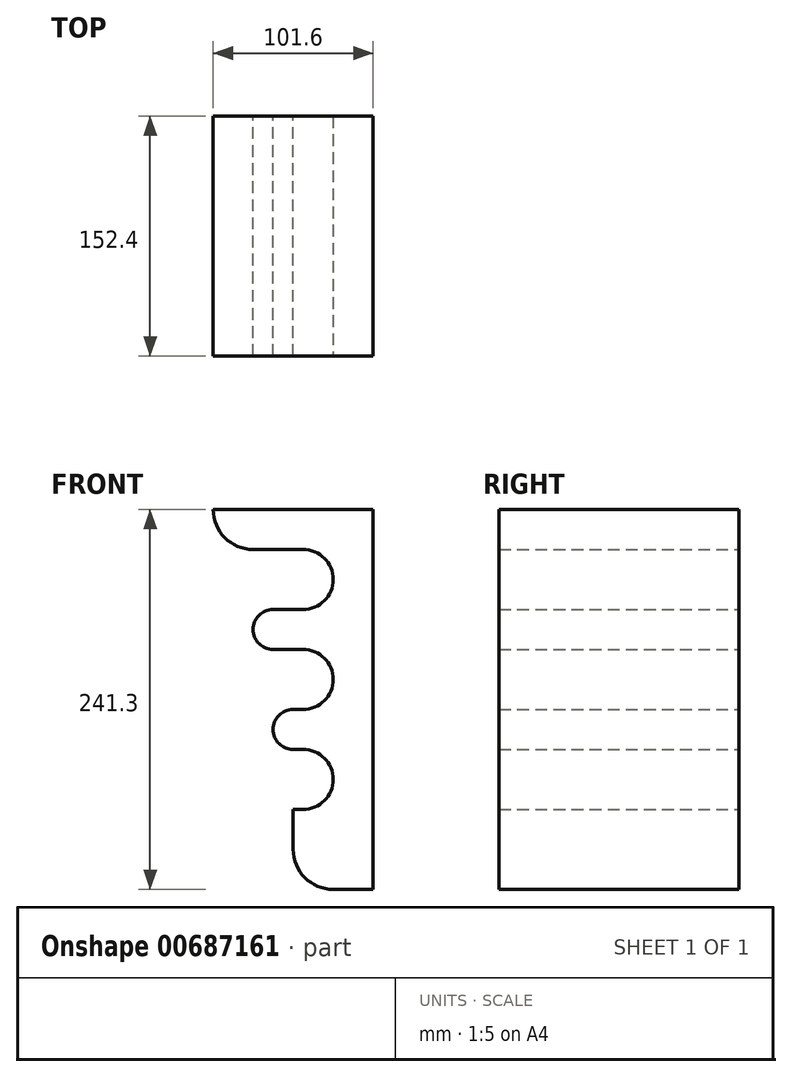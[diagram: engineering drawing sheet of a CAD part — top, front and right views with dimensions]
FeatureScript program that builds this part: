
annotation { "Feature Type Name" : "Feature", "Feature Type Description" : "" }
export const myFeature = defineFeature(function(context is Context, id is Id, definition is map)
    precondition{}
    {
        {
            var Q0;
            Q0=qCreatedBy(makeId("Front.planeOp"),FACE);
            var sketch = newSketch(context, id + "F0", { "sketchPlane" : qUnion([Q0])});
            skLineSegment(sketch, "E0.bottom", {"start": v(-172.92, 215.9) * mm, "end": v(-147.52, 215.9) * mm});
            skLineSegment(sketch, "E0.top", {"start": v(-172.92, 0) * mm, "end": v(-147.52, 0) * mm});
            skLineSegment(sketch, "E0.left", {"start": v(-172.92, 190.5) * mm, "end": v(-172.92, 152.4) * mm});
            skLineSegment(sketch, "E0.right", {"start": v(-147.52, 215.9) * mm, "end": v(-147.52, 0) * mm});
            skLineSegment(sketch, "E1.bottom", {"start": v(-147.52, 215.9) * mm, "end": v(-249.12, 215.9) * mm});
            skLineSegment(sketch, "E1.top", {"start": v(-172.92, 190.5) * mm, "end": v(-249.12, 190.5) * mm});
            skLineSegment(sketch, "E1.left", {"start": v(-147.52, 215.9) * mm, "end": v(-147.52, 190.5) * mm});
            skLineSegment(sketch, "E1.right", {"start": v(-249.12, 215.9) * mm, "end": v(-249.12, 190.5) * mm});
            skLineSegment(sketch, "E2.bottom", {"start": v(-172.92, 152.4) * mm, "end": v(-223.72, 152.4) * mm});
            skLineSegment(sketch, "E2.top", {"start": v(-172.92, 127) * mm, "end": v(-223.72, 127) * mm});
            skLineSegment(sketch, "E2.left", {"start": v(-147.52, 152.4) * mm, "end": v(-147.52, 127) * mm});
            skLineSegment(sketch, "E2.right", {"start": v(-223.72, 152.4) * mm, "end": v(-223.72, 127) * mm});
            skLineSegment(sketch, "E3.bottom", {"start": v(-172.92, 88.9) * mm, "end": v(-211.02, 88.9) * mm});
            skLineSegment(sketch, "E3.top", {"start": v(-172.92, 63.5) * mm, "end": v(-211.02, 63.5) * mm});
            skLineSegment(sketch, "E3.left", {"start": v(-147.52, 88.9) * mm, "end": v(-147.52, 63.5) * mm});
            skLineSegment(sketch, "E3.right", {"start": v(-211.02, 88.9) * mm, "end": v(-211.02, 63.5) * mm});
            skLineSegment(sketch, "E4.trimOffspring", {"start": v(-172.92, 63.5) * mm, "end": v(-172.92, 0) * mm});
            skLineSegment(sketch, "E5.trimOffspring", {"start": v(-172.92, 127) * mm, "end": v(-172.92, 88.9) * mm});
            skLineSegment(sketch, "E6.left", {"start": v(-172.92, 0) * mm, "end": v(-172.92, 25.4) * mm});
            skLineSegment(sketch, "E7.bottom", {"start": v(-172.92, 0) * mm, "end": v(-198.32, 0) * mm});
            skLineSegment(sketch, "E7.top", {"start": v(-172.92, 25.4) * mm, "end": v(-198.32, 25.4) * mm});
            skLineSegment(sketch, "E7.right", {"start": v(-198.32, 0) * mm, "end": v(-198.32, 25.4) * mm});
            skPoint(sketch, "E8.oppositeSnap0", {"position": v(-160.22, 0) * mm});
            skLineSegment(sketch, "E8.bottom", {"start": v(-147.52, 0) * mm, "end": v(-160.22, 0) * mm});
            skLineSegment(sketch, "E8.top", {"start": v(-147.52, -25.4) * mm, "end": v(-160.22, -25.4) * mm});
            skLineSegment(sketch, "E8.left", {"start": v(-147.52, 0) * mm, "end": v(-147.52, -25.4) * mm});
            skLineSegment(sketch, "E8.right", {"start": v(-160.22, 0) * mm, "end": v(-160.22, -25.4) * mm});
            skSolve(sketch);
        }
        {
            var Q0;
            Q0 = qSketchRegion(id + "F0", true);
            extrude(context, id + "F1", {"entities" : qUnion([Q0]), "depth" : 152.4 * mm, "offsetDistance" : 25.4 * mm});
        }
        {
            var Q0;
            Q0=makeQuery(id+"F1.opExtrude","SWEPT_FACE",FACE,{"disambiguationData":[OSD([sQuery(id+"F0.wireOp",EDGE,"E8.right")])]});
            var sketch = newSketch(context, id + "F2", { "sketchPlane" : qUnion([Q0])});
            skLineSegment(sketch, "E9.bottom", {"start": v(0, 0) * mm, "end": v(152.4, 0) * mm});
            skLineSegment(sketch, "E9.top", {"start": v(0, -25.4) * mm, "end": v(152.4, -25.4) * mm});
            skLineSegment(sketch, "E9.left", {"start": v(0, 0) * mm, "end": v(0, -25.4) * mm});
            skLineSegment(sketch, "E9.right", {"start": v(152.4, 0) * mm, "end": v(152.4, -25.4) * mm});
            skSolve(sketch);
        }
        {
            var Q0;
            Q0 = qSketchRegion(id + "F2", true);
            extrude(context, id + "F3", {"entities" : qUnion([Q0]), "operationType" : NewBodyOperationType.ADD, "depth" : 38.1 * mm, "offsetDistance" : 25.4 * mm});
        }
        {
            var Q0;
            Q0=makeQuery(id+"F3.opExtrude","CAP_EDGE",EDGE,{"disambiguationData":[OSD([sQuery(id+"F2.wireOp",EDGE,"E9.top")])],"isStart":false});
            fillet(context, id + "F4", {"entities" : qUnion([Q0]), "radius" : 25.4 * mm, "tangentPropagation" : true, "allowEdgeOverflow" : false});
        }
        {
            var Q0;
            Q0=makeQuery(id+"F3.boolean.opBoolean","MERGE",FACE,{"derivedFrom":[makeQuery(id+"F1.opExtrude","CAP_FACE",FACE,{"disambiguationData":[OSD([sQuery(id+"F0.wireOp",EDGE,"E0.top"),sQuery(id+"F0.wireOp",EDGE,"E0.left"),sQuery(id+"F0.wireOp",EDGE,"E0.right"),sQuery(id+"F0.wireOp",EDGE,"E1.bottom"),sQuery(id+"F0.wireOp",EDGE,"E1.top"),sQuery(id+"F0.wireOp",EDGE,"E1.left"),sQuery(id+"F0.wireOp",EDGE,"E1.right"),sQuery(id+"F0.wireOp",EDGE,"E2.bottom"),sQuery(id+"F0.wireOp",EDGE,"E2.top"),sQuery(id+"F0.wireOp",EDGE,"E2.left"),sQuery(id+"F0.wireOp",EDGE,"E2.right"),sQuery(id+"F0.wireOp",EDGE,"E3.bottom"),sQuery(id+"F0.wireOp",EDGE,"E3.top"),sQuery(id+"F0.wireOp",EDGE,"E3.left"),sQuery(id+"F0.wireOp",EDGE,"E3.right"),sQuery(id+"F0.wireOp",EDGE,"E4.trimOffspring"),sQuery(id+"F0.wireOp",EDGE,"E5.trimOffspring"),sQuery(id+"F0.wireOp",EDGE,"E7.bottom"),sQuery(id+"F0.wireOp",EDGE,"E7.top"),sQuery(id+"F0.wireOp",EDGE,"E7.right"),sQuery(id+"F0.wireOp",EDGE,"E8.top"),sQuery(id+"F0.wireOp",EDGE,"E8.left"),sQuery(id+"F0.wireOp",EDGE,"E8.right")])],"isStart":false}),makeQuery(id+"F3.opExtrude","SWEPT_FACE",FACE,{"disambiguationData":[OSD([sQuery(id+"F2.wireOp",EDGE,"E9.right")])]})]});
            var sketch = newSketch(context, id + "F5", { "sketchPlane" : qUnion([Q0])});
            skLineSegment(sketch, "E10.bottom", {"start": v(-249.12, 215.9) * mm, "end": v(-147.52, 215.9) * mm});
            skLineSegment(sketch, "E10.top", {"start": v(-211.02, 254) * mm, "end": v(-147.52, 254) * mm});
            skLineSegment(sketch, "E10.left", {"start": v(-249.12, 215.9) * mm, "end": v(-249.12, 215.9) * mm});
            skLineSegment(sketch, "E10.right", {"start": v(-147.52, 215.9) * mm, "end": v(-147.52, 254) * mm});
            skPoint(sketch, "E11.visualSharp", {"position": v(-249.12, 254) * mm});
            skArc(sketch, "E11.filletArc", {"start": v(-211.02, 254) * mm, "mid": v(-237.96, 242.84) * mm, "end": v(-249.12, 215.9) * mm});
            skSolve(sketch);
        }
        {
            var Q0;
            Q0=makeQuery(id+"F5.imprint","IMPRINT",FACE,{"disambiguationData":[TD([[makeQuery(id+"F5.imprint","IMPRINT",EDGE,{"derivedFrom":sQuery(id+"F5.wireOp",EDGE,"E10.bottom")}),-1.0]])]});
            extrude(context, id + "F6", {"entities" : qUnion([Q0]), "operationType" : NewBodyOperationType.ADD, "oppositeDirection" : true, "depth" : 151.9 * mm, "offsetDistance" : 25.4 * mm});
        }
        {
            var Q0;
            Q0=makeQuery(id+"F1.opExtrude","SWEPT_EDGE",EDGE,{"disambiguationData":[OSD([sQuery(id+"F0.wireOp",EDGE,"E3.bottom"),sQuery(id+"F0.wireOp",EDGE,"E5.trimOffspring")])]});
            fillet(context, id + "F7", {"entities" : qUnion([Q0]), "radius" : 19.05 * mm, "tangentPropagation" : true, "allowEdgeOverflow" : false});
        }
        {
            var Q0;
            Q0=makeQuery(id+"F1.opExtrude","SWEPT_EDGE",EDGE,{"disambiguationData":[OSD([sQuery(id+"F0.wireOp",EDGE,"E0.left"),sQuery(id+"F0.wireOp",EDGE,"E1.top")])]});
            var Q1;
            Q1=makeQuery(id+"F1.opExtrude","SWEPT_EDGE",EDGE,{"disambiguationData":[OSD([sQuery(id+"F0.wireOp",EDGE,"E2.top"),sQuery(id+"F0.wireOp",EDGE,"E5.trimOffspring")])]});
            fillet(context, id + "F8", {"entities" : qUnion([Q0, Q1]), "radius" : 19.05 * mm, "tangentPropagation" : true, "allowEdgeOverflow" : false});
        }
        {
            var Q0;
            Q0=makeQuery(id+"F1.opExtrude","SWEPT_EDGE",EDGE,{"disambiguationData":[OSD([sQuery(id+"F0.wireOp",EDGE,"E0.left"),sQuery(id+"F0.wireOp",EDGE,"E2.bottom")])]});
            var Q1;
            Q1=makeQuery(id+"F1.opExtrude","SWEPT_EDGE",EDGE,{"disambiguationData":[OSD([sQuery(id+"F0.wireOp",EDGE,"E4.trimOffspring"),sQuery(id+"F0.wireOp",EDGE,"E7.top"),sQuery(id+"F0.wireOp",EDGE,"E6.left")])]});
            var Q2;
            Q2=makeQuery(id+"F1.opExtrude","SWEPT_EDGE",EDGE,{"disambiguationData":[OSD([sQuery(id+"F0.wireOp",EDGE,"E3.top"),sQuery(id+"F0.wireOp",EDGE,"E4.trimOffspring")])]});
            fillet(context, id + "F9", {"entities" : qUnion([Q0, Q1, Q2]), "radius" : 19.05 * mm, "tangentPropagation" : true, "allowEdgeOverflow" : false});
        }
        {
            var Q0;
            Q0=makeQuery(id+"F1.opExtrude","SWEPT_EDGE",EDGE,{"disambiguationData":[OSD([sQuery(id+"F0.wireOp",EDGE,"E2.bottom"),sQuery(id+"F0.wireOp",EDGE,"E2.right")])]});
            var Q1;
            Q1=makeQuery(id+"F1.opExtrude","SWEPT_EDGE",EDGE,{"disambiguationData":[OSD([sQuery(id+"F0.wireOp",EDGE,"E2.top"),sQuery(id+"F0.wireOp",EDGE,"E2.right")])]});
            var Q2;
            Q2=makeQuery(id+"F1.opExtrude","SWEPT_EDGE",EDGE,{"disambiguationData":[OSD([sQuery(id+"F0.wireOp",EDGE,"E3.bottom"),sQuery(id+"F0.wireOp",EDGE,"E3.right")])]});
            var Q3;
            Q3=makeQuery(id+"F1.opExtrude","SWEPT_EDGE",EDGE,{"disambiguationData":[OSD([sQuery(id+"F0.wireOp",EDGE,"E3.top"),sQuery(id+"F0.wireOp",EDGE,"E3.right")])]});
            fillet(context, id + "F10", {"entities" : qUnion([Q0, Q1, Q2, Q3]), "radius" : 12.7 * mm, "tangentPropagation" : true, "allowEdgeOverflow" : false});
        }
        {
            var Q0;
            Q0=makeQuery(id+"F1.opExtrude","SWEPT_EDGE",EDGE,{"disambiguationData":[OSD([sQuery(id+"F0.wireOp",EDGE,"E1.top"),sQuery(id+"F0.wireOp",EDGE,"E1.right")])]});
            fillet(context, id + "F11", {"entities" : qUnion([Q0]), "radius" : 25.4 * mm, "tangentPropagation" : true, "allowEdgeOverflow" : false});
        }
    });
